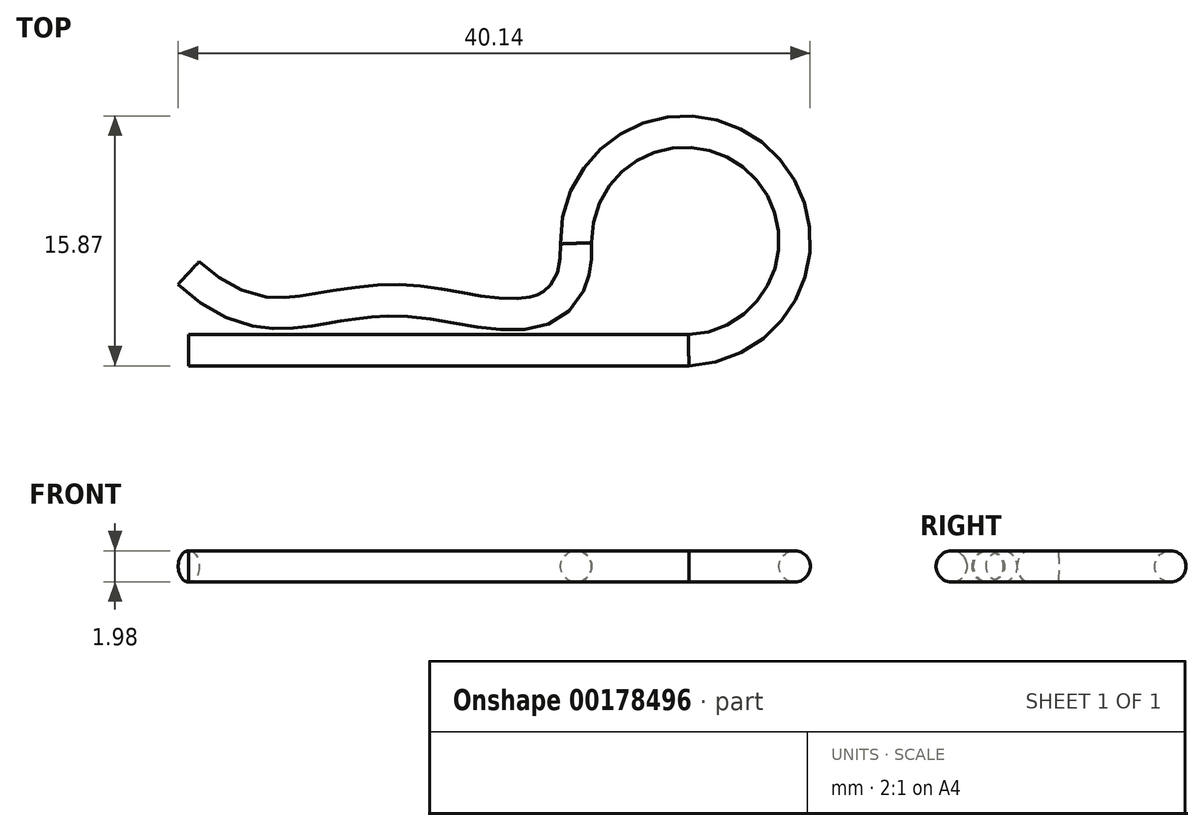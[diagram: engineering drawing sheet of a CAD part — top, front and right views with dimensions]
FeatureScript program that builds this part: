
annotation { "Feature Type Name" : "Feature", "Feature Type Description" : "" }
export const myFeature = defineFeature(function(context is Context, id is Id, definition is map)
    precondition{}
    {
        {
            var Q0;
            Q0=qCreatedBy(makeId("Top.planeOp"),FACE);
            var sketch = newSketch(context, id + "F0", { "sketchPlane" : qUnion([Q0])});
            skLineSegment(sketch, "E0", {"start": v(0, 0) * mm, "end": v(31.75, 0) * mm});
            skArc(sketch, "E1", {"start": v(31.75, 0) * mm, "mid": v(36.32, 11.98) * mm, "end": v(24.6, 6.8) * mm});
            skFitSpline(sketch, "E2", {"points": [v(24.6, 6.8) * mm, v(21.66, 2.36) * mm, v(13.24, 3.18) * mm, v(5.46, 2.36) * mm, v(0, 4.92) * mm], "startDerivative": vector(2.03, -37.9) * mm, "endDerivative": vector(-23.31, 21.36) * mm});
            skSolve(sketch);
        }
        {
            var Q0;
            Q0=qCreatedBy(makeId("Right.planeOp"),FACE);
            var sketch = newSketch(context, id + "F1", { "sketchPlane" : qUnion([Q0])});
            skCircle(sketch, "E3", {"center": v(0, 0) * mm, "radius": 1 * mm});
            skSolve(sketch);
        }
        {
            var Q0;
            Q0=makeQuery(id+"F1.imprint","IMPRINT",FACE,{"disambiguationData":[TD([[makeQuery(id+"F1.imprint","IMPRINT",EDGE,{"derivedFrom":sQuery(id+"F1.wireOp",EDGE,"E3")}),1.0]])]});
            var Q1;
            Q1=sQuery(id+"F0.wireOp",EDGE,"E0");
            var Q2;
            Q2=sQuery(id+"F0.wireOp",EDGE,"E1");
            var Q3;
            Q3=sQuery(id+"F0.wireOp",EDGE,"E2");
            sweep(context, id + "F2", {"profiles" : qUnion([Q0]), "path" : qUnion([Q1, Q2, Q3])});
        }
    });
